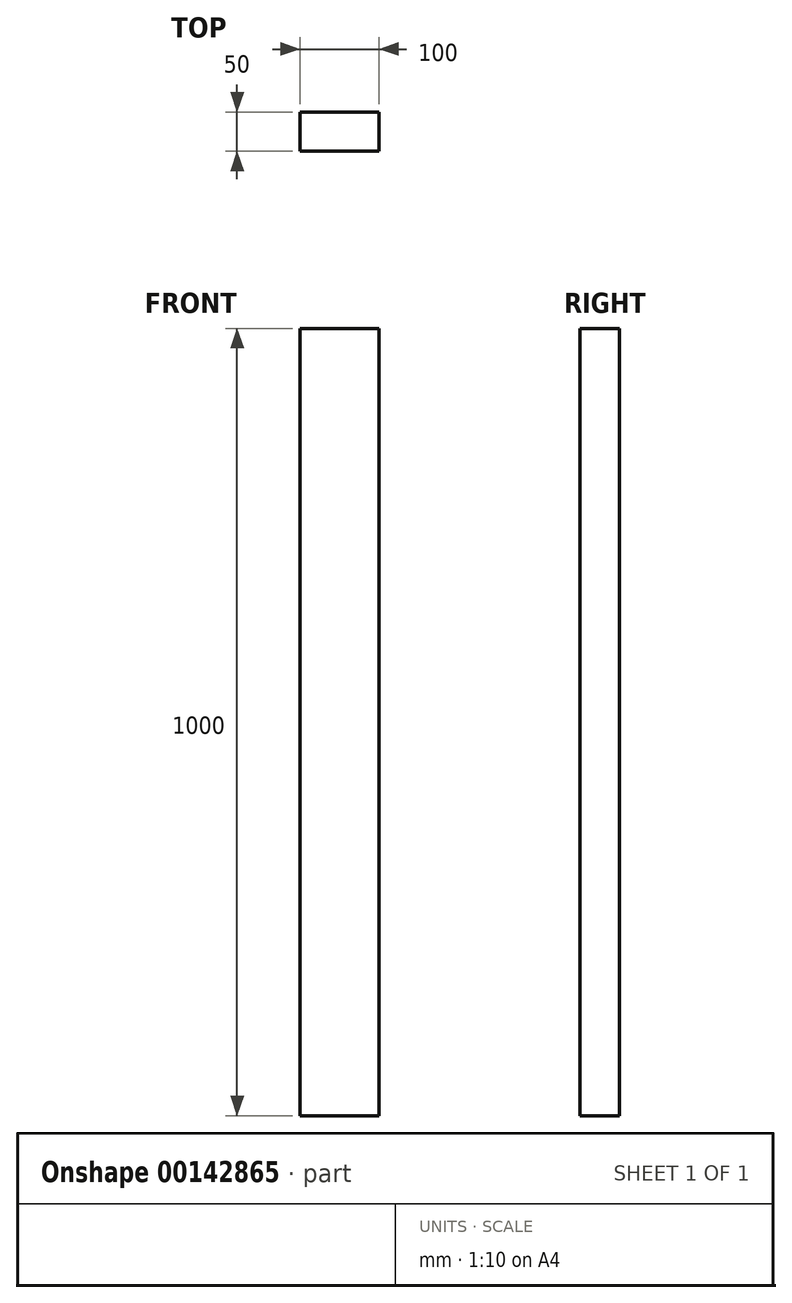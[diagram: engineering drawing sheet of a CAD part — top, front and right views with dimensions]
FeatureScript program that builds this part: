
annotation { "Feature Type Name" : "Feature", "Feature Type Description" : "" }
export const myFeature = defineFeature(function(context is Context, id is Id, definition is map)
    precondition{}
    {
        {
            var Q0;
            Q0=qCreatedBy(makeId("Top.planeOp"),FACE);
            var sketch = newSketch(context, id + "F0", { "sketchPlane" : qUnion([Q0])});
            skLineSegment(sketch, "E0.bottom", {"start": v(-50, 25) * mm, "end": v(50, 25) * mm});
            skLineSegment(sketch, "E0.top", {"start": v(-50, -25) * mm, "end": v(50, -25) * mm});
            skLineSegment(sketch, "E0.left", {"start": v(-50, 25) * mm, "end": v(-50, -25) * mm});
            skLineSegment(sketch, "E0.right", {"start": v(50, 25) * mm, "end": v(50, -25) * mm});
            skPoint(sketch, "E0.middle", {"position": v(0, 0) * mm});
            skSolve(sketch);
        }
        {
            var Q0;
            Q0=makeQuery(id+"F0.imprint","IMPRINT",FACE,{"disambiguationData":[TD([[makeQuery(id+"F0.imprint","IMPRINT",EDGE,{"derivedFrom":sQuery(id+"F0.wireOp",EDGE,"E0.bottom")}),-1.0]])]});
            extrude(context, id + "F1", {"entities" : qUnion([Q0]), "depth" : 1000 * mm});
        }
    });
